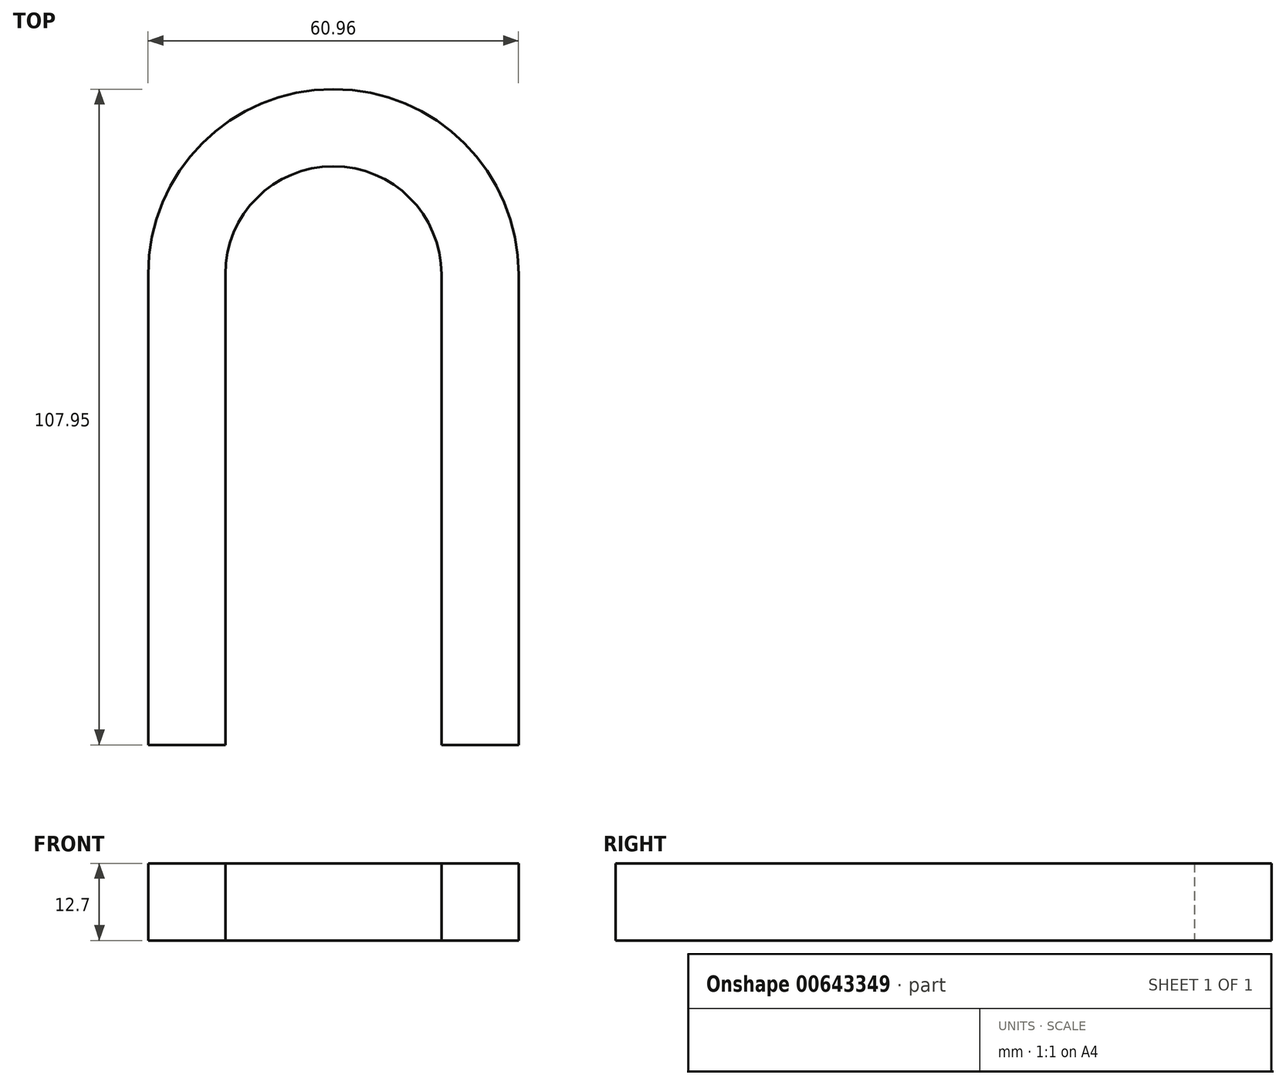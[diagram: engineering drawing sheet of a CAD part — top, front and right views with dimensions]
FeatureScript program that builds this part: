
annotation { "Feature Type Name" : "Feature", "Feature Type Description" : "" }
export const myFeature = defineFeature(function(context is Context, id is Id, definition is map)
    precondition{}
    {
        {
            var Q0;
            Q0=qCreatedBy(makeId("Top.planeOp"),FACE);
            var sketch = newSketch(context, id + "F0", { "sketchPlane" : qUnion([Q0])});
            skArc(sketch, "E0", {"start": v(6.1, 33.11) * mm, "mid": v(-11.69, 50.9) * mm, "end": v(-29.47, 33.11) * mm});
            skLineSegment(sketch, "E1", {"start": v(6.1, 33.11) * mm, "end": v(6.1, -44.36) * mm});
            skLineSegment(sketch, "E2", {"start": v(-42.17, 33.11) * mm, "end": v(-42.17, -44.36) * mm});
            skLineSegment(sketch, "E3", {"start": v(18.8, 33.11) * mm, "end": v(18.8, -44.36) * mm});
            skPoint(sketch, "E4.trimOffspring.end.orphan", {"position": v(-35.82, 33.11) * mm});
            skLineSegment(sketch, "E5.trimOffspring", {"start": v(18.8, 33.11) * mm, "end": v(24.6, 33.11) * mm});
            skArc(sketch, "E6.trimOffspring", {"start": v(18.8, 33.11) * mm, "mid": v(-11.69, 63.6) * mm, "end": v(-42.17, 33.11) * mm});
            skLineSegment(sketch, "E7", {"start": v(-42.17, -44.36) * mm, "end": v(-29.47, -44.36) * mm});
            skLineSegment(sketch, "E8", {"start": v(6.1, -44.36) * mm, "end": v(18.8, -44.36) * mm});
            skLineSegment(sketch, "E9", {"start": v(-29.47, 33.11) * mm, "end": v(-29.47, -44.36) * mm});
            skSolve(sketch);
        }
        {
            var Q0;
            Q0 = qSketchRegion(id + "F0", true);
            extrude(context, id + "F1", {"entities" : qUnion([Q0]), "depth" : 12.7 * mm, "offsetDistance" : 25.4 * mm});
        }
    });
